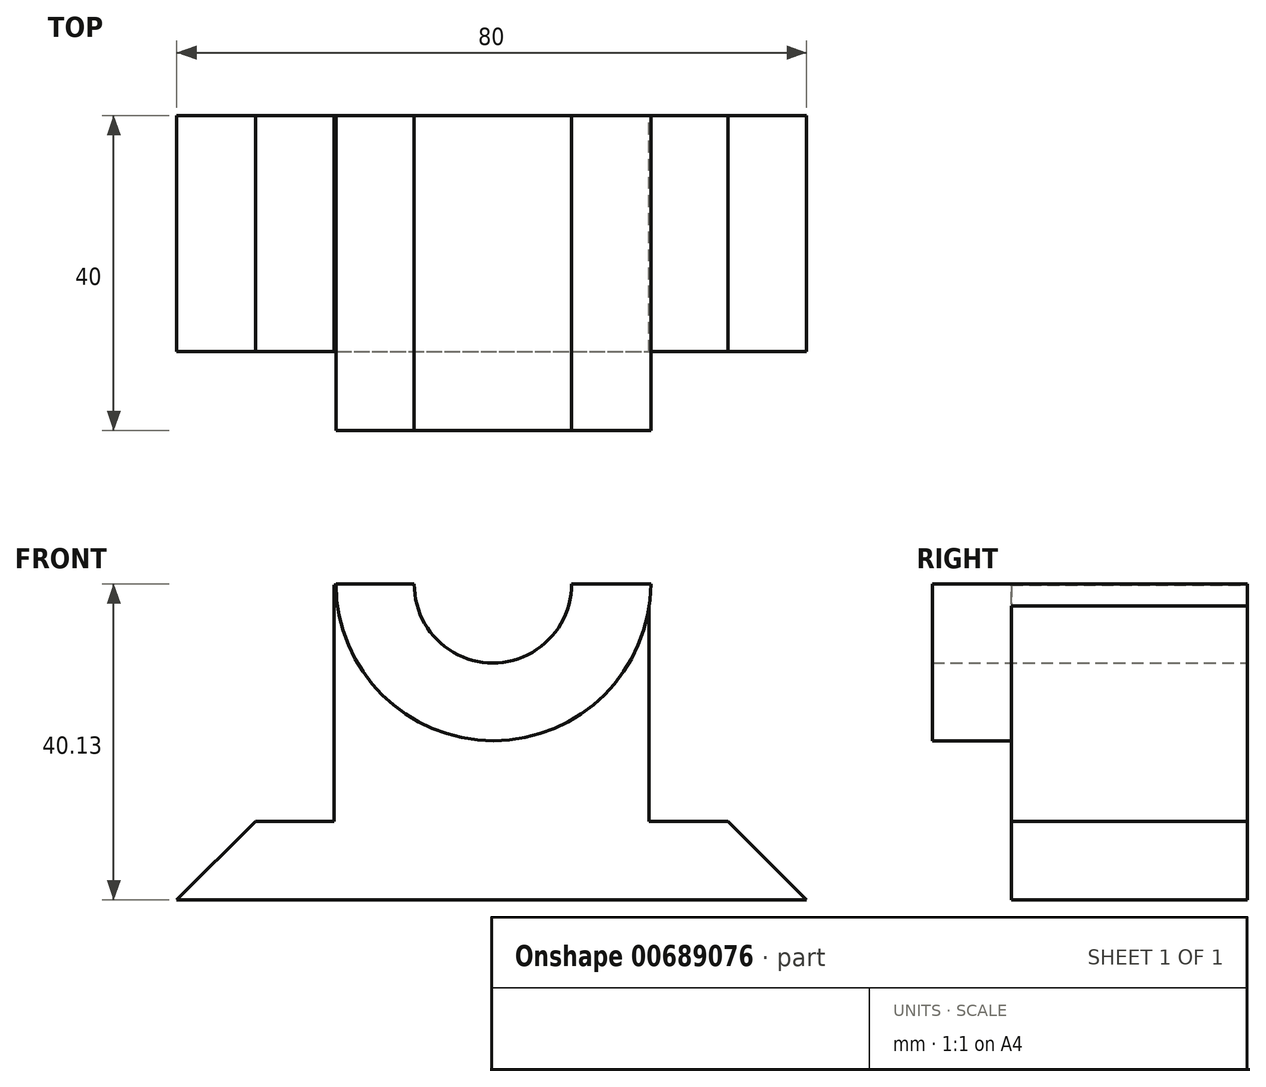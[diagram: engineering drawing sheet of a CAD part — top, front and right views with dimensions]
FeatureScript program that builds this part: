
annotation { "Feature Type Name" : "Feature", "Feature Type Description" : "" }
export const myFeature = defineFeature(function(context is Context, id is Id, definition is map)
    precondition{}
    {
        {
            var Q0;
            Q0=qCreatedBy(makeId("Front.planeOp"),FACE);
            var sketch = newSketch(context, id + "F0", { "sketchPlane" : qUnion([Q0])});
            skLineSegment(sketch, "E0", {"start": v(-65.28, 0) * mm, "end": v(14.72, 0) * mm});
            skLineSegment(sketch, "E1", {"start": v(14.72, 0) * mm, "end": v(-65.28, 0) * mm});
            skLineSegment(sketch, "E2", {"start": v(-65.28, 0) * mm, "end": v(-55.28, 10) * mm});
            skLineSegment(sketch, "E3", {"start": v(-55.28, 10) * mm, "end": v(-45.28, 10) * mm});
            skLineSegment(sketch, "E4", {"start": v(-45.28, 10) * mm, "end": v(-45.28, 40) * mm});
            skLineSegment(sketch, "E5", {"start": v(-45.28, 40) * mm, "end": v(-5.28, 40) * mm});
            skLineSegment(sketch, "E6", {"start": v(-5.28, 40) * mm, "end": v(-5.28, 10) * mm});
            skLineSegment(sketch, "E7", {"start": v(-5.28, 10) * mm, "end": v(4.72, 10) * mm});
            skLineSegment(sketch, "E8", {"start": v(4.72, 10) * mm, "end": v(14.72, 0) * mm});
            skSolve(sketch);
        }
        {
            var Q0;
            Q0 = qSketchRegion(id + "F0", true);
            extrude(context, id + "F1", {"entities" : qUnion([Q0]), "depth" : 30 * mm, "offsetDistance" : 25 * mm});
        }
        {
            var Q0;
            Q0=qCreatedBy(makeId("Front.planeOp"),FACE);
            var sketch = newSketch(context, id + "F2", { "sketchPlane" : qUnion([Q0])});
            skLineSegment(sketch, "E9", {"start": v(-45.07, 40.22) * mm, "end": v(-25.07, 40.22) * mm});
            skCircle(sketch, "E10", {"center": v(-25.07, 40.22) * mm, "radius": 20 * mm});
            skSolve(sketch);
        }
        {
            var Q0;
            Q0 = qSketchRegion(id + "F2", true);
            extrude(context, id + "F3", {"entities" : qUnion([Q0]), "operationType" : NewBodyOperationType.ADD, "depth" : 40 * mm, "offsetDistance" : 25 * mm});
        }
        {
            var Q0;
            Q0=qCreatedBy(makeId("Front.planeOp"),FACE);
            var sketch = newSketch(context, id + "F4", { "sketchPlane" : qUnion([Q0])});
            skLineSegment(sketch, "E11", {"start": v(-45.13, 40.11) * mm, "end": v(-25.13, 40.11) * mm});
            skCircle(sketch, "E12", {"center": v(-25.13, 40.11) * mm, "radius": 10 * mm});
            skSolve(sketch);
        }
        {
            var Q0;
            Q0 = qSketchRegion(id + "F4", true);
            extrude(context, id + "F5", {"entities" : qUnion([Q0]), "operationType" : NewBodyOperationType.REMOVE, "depth" : 50.6 * mm, "offsetDistance" : 25 * mm});
        }
        {
            var Q0;
            Q0=qCreatedBy(makeId("Front.planeOp"),FACE);
            var sketch = newSketch(context, id + "F6", { "sketchPlane" : qUnion([Q0])});
            skLineSegment(sketch, "E13", {"start": v(-45.6, 40.13) * mm, "end": v(-1.9, 40.13) * mm});
            skLineSegment(sketch, "E14", {"start": v(-1.9, 40.13) * mm, "end": v(-3.92, 66.29) * mm});
            skLineSegment(sketch, "E15", {"start": v(-3.92, 66.29) * mm, "end": v(-46, 66.29) * mm});
            skLineSegment(sketch, "E16", {"start": v(-46, 66.29) * mm, "end": v(-45.6, 40.13) * mm});
            skSolve(sketch);
        }
        {
            var Q0;
            Q0 = qSketchRegion(id + "F6", true);
            extrude(context, id + "F7", {"entities" : qUnion([Q0]), "operationType" : NewBodyOperationType.REMOVE, "depth" : 72.9 * mm, "offsetDistance" : 25 * mm});
        }
    });
